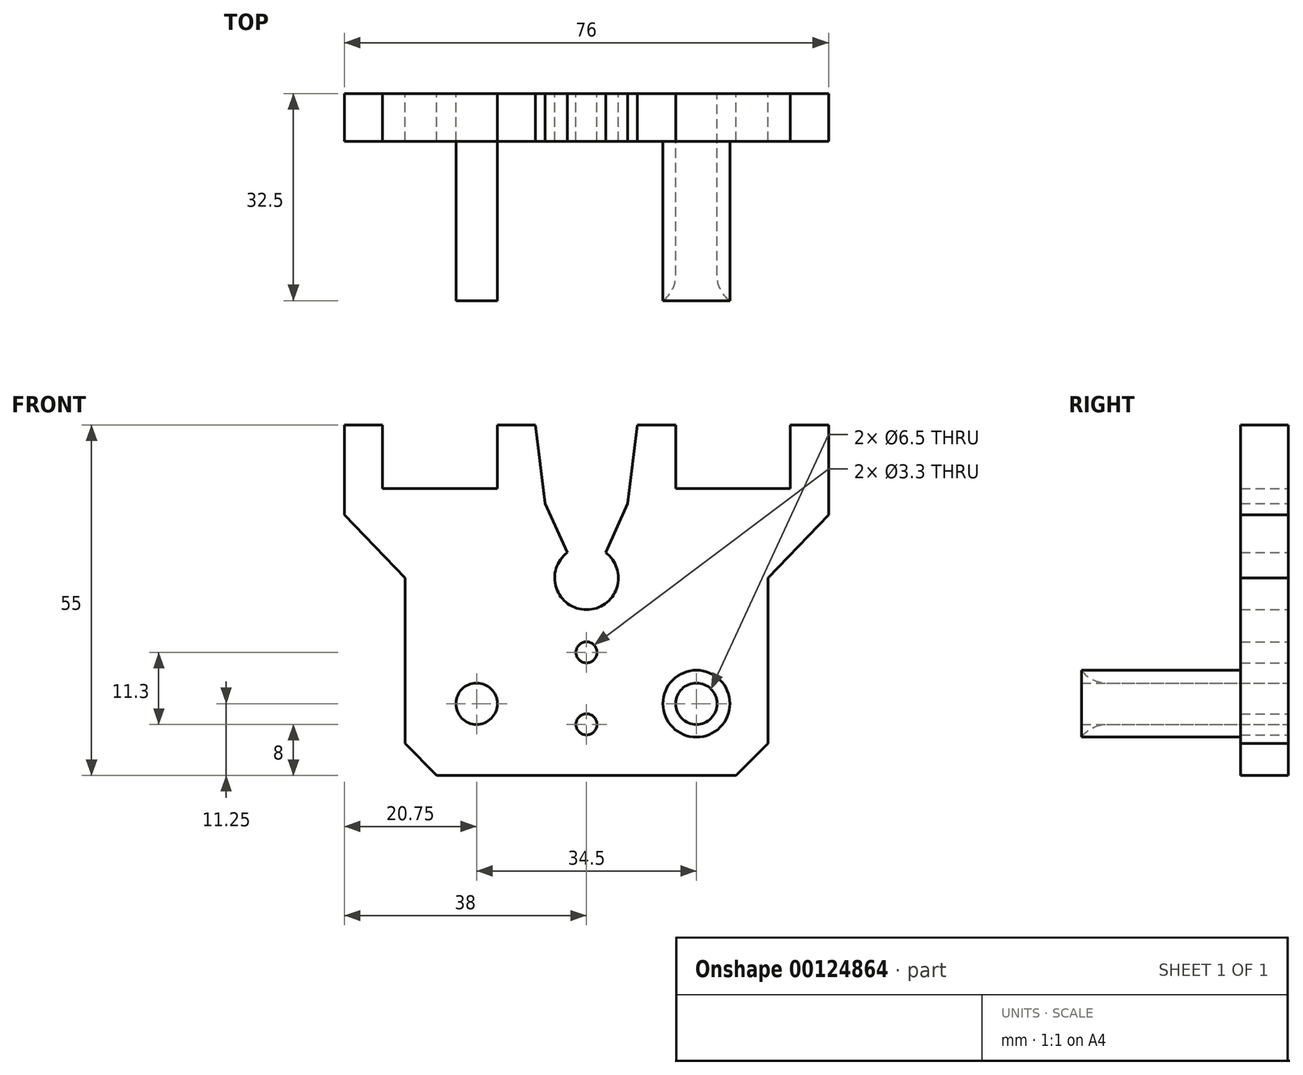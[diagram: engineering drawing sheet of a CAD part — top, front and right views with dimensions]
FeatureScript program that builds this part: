
annotation { "Feature Type Name" : "Feature", "Feature Type Description" : "" }
export const myFeature = defineFeature(function(context is Context, id is Id, definition is map)
    precondition{}
    {
        {
            var Q0;
            Q0=qCreatedBy(makeId("Front.planeOp"),FACE);
            var sketch = newSketch(context, id + "F0", { "sketchPlane" : qUnion([Q0])});
            skLineSegment(sketch, "E0", {"start": v(-28.5, 0) * mm, "end": v(28.5, 0) * mm, "construction": true});
            skLineSegment(sketch, "E1", {"start": v(-23.5, -5) * mm, "end": v(23.5, -5) * mm});
            skLineSegment(sketch, "E2", {"start": v(-28.5, 0) * mm, "end": v(-23.5, -5) * mm});
            skLineSegment(sketch, "E3", {"start": v(28.5, 0) * mm, "end": v(23.5, -5) * mm});
            skLineSegment(sketch, "E4", {"start": v(0, 69.6) * mm, "end": v(0, -73.57) * mm, "construction": true});
            skLineSegment(sketch, "E5", {"start": v(134.78, 0) * mm, "end": v(-161.89, 0) * mm, "construction": true});
            skLineSegment(sketch, "E6", {"start": v(-28.5, 0) * mm, "end": v(-28.5, 26) * mm});
            skLineSegment(sketch, "E7", {"start": v(28.5, 0) * mm, "end": v(28.5, 26) * mm});
            skLineSegment(sketch, "E8", {"start": v(-28.5, 26) * mm, "end": v(28.5, 26) * mm, "construction": true});
            skCircle(sketch, "E9", {"center": v(0, 26) * mm, "radius": 5 * mm});
            skLineSegment(sketch, "E10", {"start": v(-28.5, 26) * mm, "end": v(-38, 35.9) * mm});
            skLineSegment(sketch, "E11", {"start": v(28.5, 26) * mm, "end": v(38, 35.9) * mm});
            skPoint(sketch, "E12", {"position": v(0, 50) * mm});
            skLineSegment(sketch, "E13", {"start": v(-38, 50) * mm, "end": v(-38, 35.9) * mm});
            skLineSegment(sketch, "E14", {"start": v(38, 50) * mm, "end": v(38, 35.9) * mm});
            skLineSegment(sketch, "E15", {"start": v(38, 50) * mm, "end": v(32, 50) * mm});
            skLineSegment(sketch, "E16", {"start": v(32, 50) * mm, "end": v(32, 40) * mm});
            skLineSegment(sketch, "E17", {"start": v(-38, 50) * mm, "end": v(-32, 50) * mm});
            skLineSegment(sketch, "E18", {"start": v(-32, 50) * mm, "end": v(-32, 40) * mm});
            skLineSegment(sketch, "E19", {"start": v(-32, 40) * mm, "end": v(-14, 40) * mm});
            skLineSegment(sketch, "E20", {"start": v(-14, 40) * mm, "end": v(-14, 50) * mm});
            skLineSegment(sketch, "E21", {"start": v(-14, 50) * mm, "end": v(-8, 50) * mm});
            skLineSegment(sketch, "E22", {"start": v(-8, 50) * mm, "end": v(-4.96, 25.39) * mm});
            skLineSegment(sketch, "E23", {"start": v(32, 40) * mm, "end": v(14, 40) * mm});
            skLineSegment(sketch, "E24", {"start": v(14, 40) * mm, "end": v(14, 50) * mm});
            skLineSegment(sketch, "E25", {"start": v(14, 50) * mm, "end": v(8, 50) * mm});
            skLineSegment(sketch, "E26", {"start": v(8, 50) * mm, "end": v(4.96, 25.39) * mm});
            skPoint(sketch, "E27", {"position": v(0, 3) * mm});
            skPoint(sketch, "E28", {"position": v(0, -5) * mm});
            skPoint(sketch, "E29", {"position": v(0, 14.3) * mm});
            skCircle(sketch, "E30", {"center": v(0, 3) * mm, "radius": 1.65 * mm});
            skPoint(sketch, "E31", {"position": v(0, 4.65) * mm});
            skCircle(sketch, "E32", {"center": v(0, 14.3) * mm, "radius": 1.65 * mm});
            skPoint(sketch, "E33", {"position": v(0, 12.65) * mm});
            skLineSegment(sketch, "E34", {"start": v(-6.48, 37.7) * mm, "end": v(-3, 30) * mm});
            skLineSegment(sketch, "E35", {"start": v(6.48, 37.7) * mm, "end": v(3, 30) * mm});
            skPoint(sketch, "E36", {"position": v(0, 31) * mm});
            skLineSegment(sketch, "E37", {"start": v(-3, 30) * mm, "end": v(3, 30) * mm, "construction": true});
            skCircle(sketch, "E38", {"center": v(17.25, 6.25) * mm, "radius": 3.25 * mm});
            skLineSegment(sketch, "E39", {"start": v(17.25, 14.18) * mm, "end": v(17.25, 3) * mm, "construction": true});
            skLineSegment(sketch, "E40", {"start": v(20.5, 6.25) * mm, "end": v(17.25, 6.25) * mm, "construction": true});
            skCircle(sketch, "E41.MirrorC", {"center": v(-17.25, 6.25) * mm, "radius": 3.25 * mm});
            skSolve(sketch);
        }
        {
            var Q0;
            {var subQ3=sQuery(id+"F0.wireOp",EDGE,"E34");Q0=makeQuery(id+"F0.imprint","IMPRINT",FACE,{"disambiguationData":[TD([[makeQuery(id+"F0.imprint","IMPRINT",EDGE,{"derivedFrom":subQ3}),-1.0]])]});}
            var Q1;
            {var subQ3=sQuery(id+"F0.wireOp",EDGE,"E35");Q1=makeQuery(id+"F0.imprint","IMPRINT",FACE,{"disambiguationData":[TD([[makeQuery(id+"F0.imprint","IMPRINT",EDGE,{"derivedFrom":subQ3}),1.0]])]});}
            var Q2;
            Q2=makeQuery(id+"F0.imprint","IMPRINT",FACE,{"disambiguationData":[TD([[makeQuery(id+"F0.imprint","IMPRINT",EDGE,{"derivedFrom":sQuery(id+"F0.wireOp",EDGE,"E1")}),1.0]])]});
            extrude(context, id + "F1", {"entities" : qUnion([Q0, Q1, Q2]), "depth" : 7.5 * mm});
        }
        {
            var Q0;
            Q0=makeQuery(id+"F1.opExtrude","CAP_FACE",FACE,{"disambiguationData":[OSD([sQuery(id+"F0.wireOp",EDGE,"E1"),sQuery(id+"F0.wireOp",EDGE,"E2"),sQuery(id+"F0.wireOp",EDGE,"E3"),sQuery(id+"F0.wireOp",EDGE,"E6"),sQuery(id+"F0.wireOp",EDGE,"E7"),sQuery(id+"F0.wireOp",EDGE,"E9"),sQuery(id+"F0.wireOp",EDGE,"E10"),sQuery(id+"F0.wireOp",EDGE,"E11"),sQuery(id+"F0.wireOp",EDGE,"E13"),sQuery(id+"F0.wireOp",EDGE,"E14"),sQuery(id+"F0.wireOp",EDGE,"E15"),sQuery(id+"F0.wireOp",EDGE,"E16"),sQuery(id+"F0.wireOp",EDGE,"E17"),sQuery(id+"F0.wireOp",EDGE,"E18"),sQuery(id+"F0.wireOp",EDGE,"E19"),sQuery(id+"F0.wireOp",EDGE,"E20"),sQuery(id+"F0.wireOp",EDGE,"E21"),sQuery(id+"F0.wireOp",EDGE,"E22"),sQuery(id+"F0.wireOp",EDGE,"E23"),sQuery(id+"F0.wireOp",EDGE,"E24"),sQuery(id+"F0.wireOp",EDGE,"E25"),sQuery(id+"F0.wireOp",EDGE,"E26"),sQuery(id+"F0.wireOp",EDGE,"IbvsripJ-33sL-cfCT-cYSY-9IWthU5eTFzF"),sQuery(id+"F0.wireOp",EDGE,"qa8JPh8N-UMUc-5UMx-rpRC-zUcu6IydsLNG"),sQuery(id+"F0.wireOp",EDGE,"E30"),sQuery(id+"F0.wireOp",EDGE,"E32"),sQuery(id+"F0.wireOp",EDGE,"E34"),sQuery(id+"F0.wireOp",EDGE,"E35")])],"isStart":false});
            var sketch = newSketch(context, id + "F2", { "sketchPlane" : qUnion([Q0])});
            skLineSegment(sketch, "E42.0", {"start": v(-23.5, -5) * mm, "end": v(23.5, -5) * mm});
            skArc(sketch, "E43.0", {"start": v(-3, 30) * mm, "mid": v(0, 21) * mm, "end": v(3, 30) * mm});
            skLineSegment(sketch, "E44", {"start": v(0, 47.33) * mm, "end": v(0, -7.62) * mm, "construction": true});
            skCircle(sketch, "E45.0", {"center": v(17.25, 6.25) * mm, "radius": 3.25 * mm});
            skCircle(sketch, "E45.1", {"center": v(-17.25, 6.25) * mm, "radius": 3.25 * mm});
            skCircle(sketch, "E46", {"center": v(-17.25, 6.25) * mm, "radius": 5.25 * mm});
            skCircle(sketch, "E47", {"center": v(17.25, 6.25) * mm, "radius": 5.25 * mm});
            skSolve(sketch);
        }
        {
            var Q0;
            Q0=makeQuery(id+"F2.imprint","IMPRINT",FACE,{"disambiguationData":[TD([[makeQuery(id+"F2.imprint","IMPRINT",EDGE,{"derivedFrom":sQuery(id+"F2.wireOp",EDGE,"E45.1")}),1.0]])]});
            var Q1;
            Q1=makeQuery(id+"F2.imprint","IMPRINT",FACE,{"disambiguationData":[TD([[makeQuery(id+"F2.imprint","IMPRINT",EDGE,{"derivedFrom":sQuery(id+"F2.wireOp",EDGE,"E45.0")}),-1.0]])]});
            extrude(context, id + "F3", {"entities" : qUnion([Q0, Q1]), "operationType" : NewBodyOperationType.ADD, "depth" : 25 * mm});
        }
        {
            var Q0;
            Q0=makeQuery(id+"F3.opExtrude","CAP_EDGE",EDGE,{"disambiguationData":[OSD([sQuery(id+"F2.wireOp",EDGE,"E46")])],"isStart":true});
            var Q1;
            Q1=makeQuery(id+"F3.opExtrude","CAP_EDGE",EDGE,{"disambiguationData":[OSD([sQuery(id+"F2.wireOp",EDGE,"E47")])],"isStart":true});
            var Q2;
            Q2=makeQuery(id+"F3.opExtrude","CAP_EDGE",EDGE,{"disambiguationData":[OSD([sQuery(id+"F2.wireOp",EDGE,"E45.1")])],"isStart":false});
            var Q3;
            Q3=makeQuery(id+"F3.opExtrude","CAP_EDGE",EDGE,{"disambiguationData":[OSD([sQuery(id+"F2.wireOp",EDGE,"E45.0")])],"isStart":false});
            fillet(context, id + "F4", {"entities" : qUnion([Q0, Q1, Q2, Q3]), "radius" : 5 * mm, "tangentPropagation" : true, "allowEdgeOverflow" : false});
        }
    });
